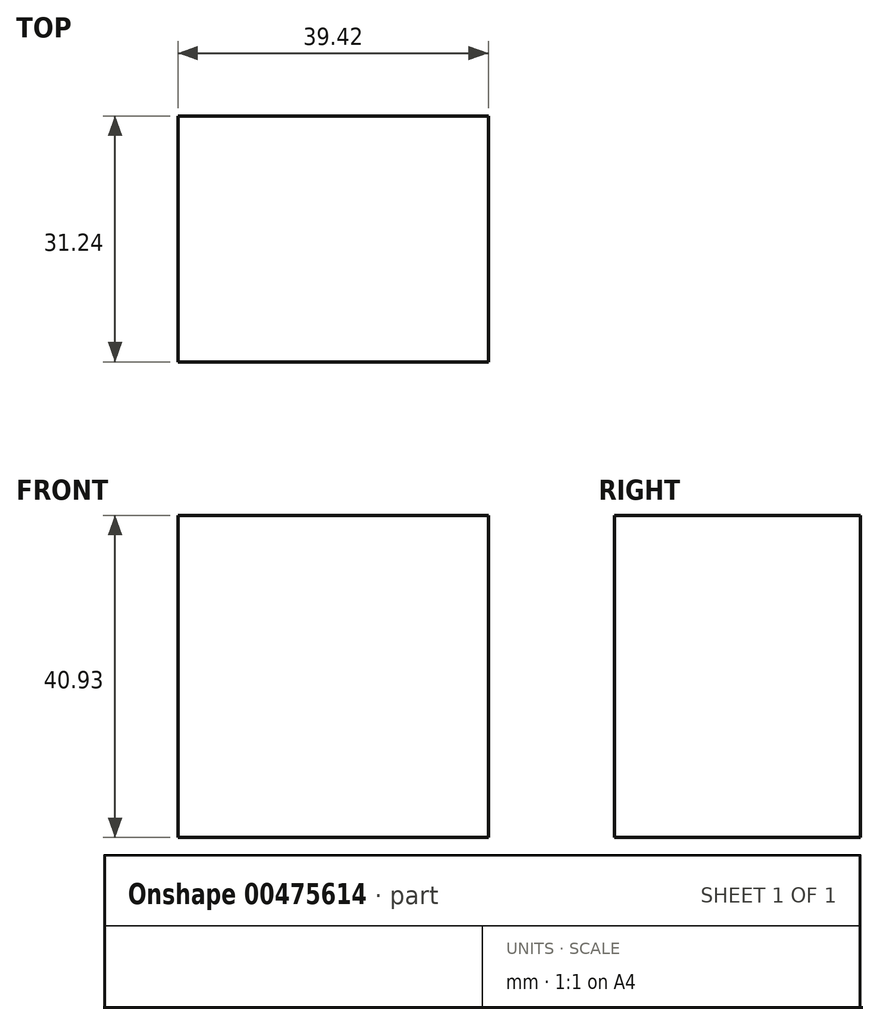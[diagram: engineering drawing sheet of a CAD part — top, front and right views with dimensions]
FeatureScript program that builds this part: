
annotation { "Feature Type Name" : "Feature", "Feature Type Description" : "" }
export const myFeature = defineFeature(function(context is Context, id is Id, definition is map)
    precondition{}
    {
        {
            var Q0;
            Q0=qCreatedBy(makeId("Front.planeOp"),FACE);
            var sketch = newSketch(context, id + "F0", { "sketchPlane" : qUnion([Q0])});
            skLineSegment(sketch, "E0.bottom", {"start": v(-60.63, 31.66) * mm, "end": v(-21.21, 31.66) * mm});
            skLineSegment(sketch, "E0.top", {"start": v(-60.63, -9.27) * mm, "end": v(-21.21, -9.27) * mm});
            skLineSegment(sketch, "E0.left", {"start": v(-60.63, 31.66) * mm, "end": v(-60.63, -9.27) * mm});
            skLineSegment(sketch, "E0.right", {"start": v(-21.21, 31.66) * mm, "end": v(-21.21, -9.27) * mm});
            skSolve(sketch);
        }
        {
            var Q0;
            Q0 = qSketchRegion(id + "F0", true);
            extrude(context, id + "F1", {"entities" : qUnion([Q0]), "depth" : 31.24 * mm});
        }
    });
